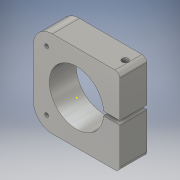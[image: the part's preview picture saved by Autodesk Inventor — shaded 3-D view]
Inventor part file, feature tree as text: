
AUTODESK INVENTOR PART (.ipt)
format: ipt  version: 2016 (Build 200138000, 138)  size: 337,408 bytes
history: native  units: in
note: dims shown in document units (in); Inventor stores cm internally (conversion verified against a paired STEP export)
features: sketch x6, extrude x2, hole x2, projected_geometry x2
ambient origin geometry x8: Origin, YZ Plane, XZ Plane, XY Plane, X Axis, Y Axis, Z Axis, Center Point
bodies: Solid1 (feature_tree)
feature tree (12):
  extrude  "Extrusion1"  Depth=2.25in
  hole  "Hole1"  [1 undecoded]
  hole  "Hole2"  [1 undecoded]
  sketch  "Sketch4"  dims[d8=1.125in d11=2.25in]
  sketch  "Sketch5"  dims[d12=0.7in d13=0.0in]
  extrude  "Extrusion2"  Depth=2.25in
  sketch  "Sketch1"  dims[d0=2.25in d1=2.25in]
  sketch  "Sketch2"  dims[d2=0.5in d3=0.125in]
  projected_geometry  "Projected Loop1"
  sketch  "Sketch3"  dims[d5=0.4in d6=0.408in]
  sketch  "Sketch6"  dims[d14=0.1in d15=0.1in d16=0.1in d17=0.75in d18=0.375in d19=0.25in d20=0.5635in d21=1.0in d22=0.8108in d23=1.415in d24=0.16in d25=0.75in d26=0.3in d27=0.25in d28=0.5635in d29=1.0in d30=0.8108in d31=0.1in d32=0.15in d33=0.15in d34=0.1in d35=0.15in d36=0.15in d37=1.0in d38=0.0in]
  projected_geometry  "Projected Loop2"
note: 2 required parameter values undecoded (feature->parameter linkage not recoverable at this tier; creation-order binding heuristic only, values carry confidence <= 0.55)
